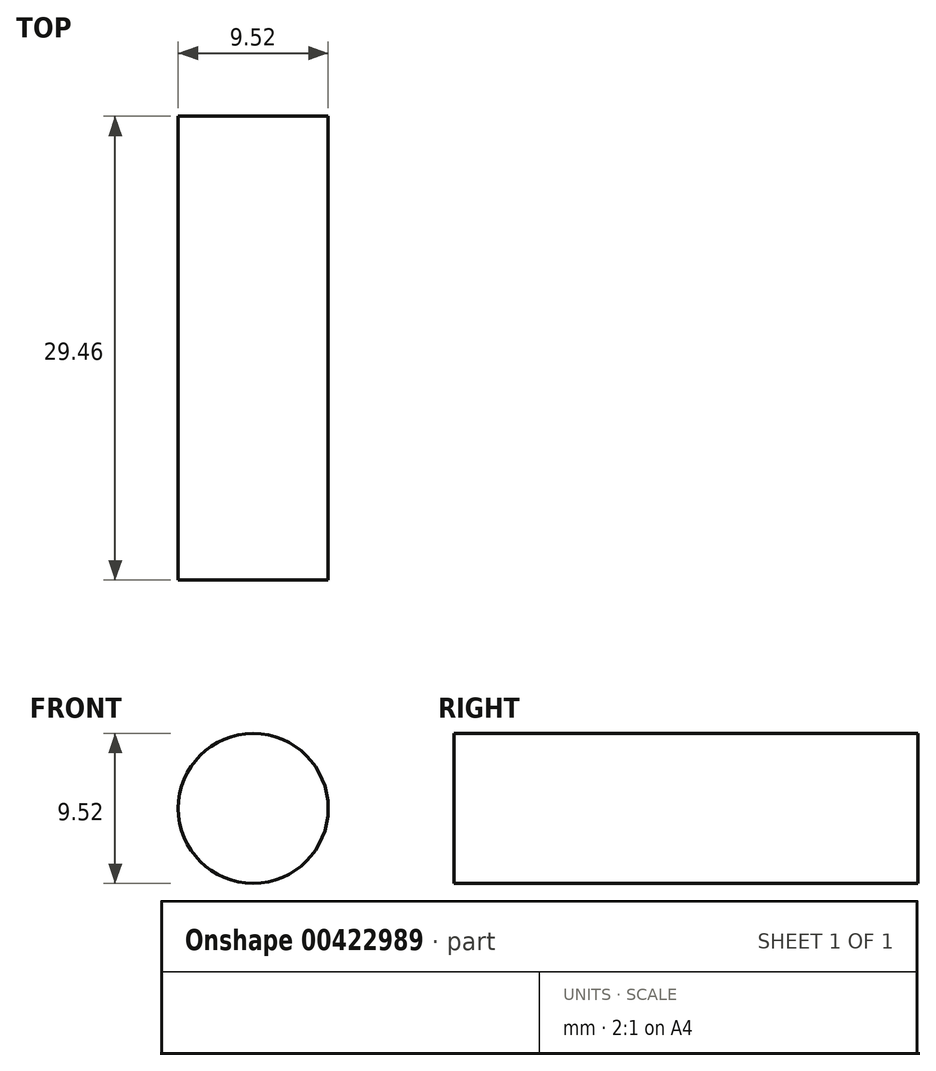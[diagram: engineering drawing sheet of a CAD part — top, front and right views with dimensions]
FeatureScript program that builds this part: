
annotation { "Feature Type Name" : "Feature", "Feature Type Description" : "" }
export const myFeature = defineFeature(function(context is Context, id is Id, definition is map)
    precondition{}
    {
        {
            var Q0;
            Q0=qCreatedBy(makeId("Front.planeOp"),FACE);
            var sketch = newSketch(context, id + "F0", { "sketchPlane" : qUnion([Q0])});
            skCircle(sketch, "E0", {"center": v(0, 0) * mm, "radius": 4.76 * mm});
            skSolve(sketch);
        }
        {
            var Q0;
            Q0 = qSketchRegion(id + "F0", true);
            extrude(context, id + "F1", {"entities" : qUnion([Q0]), "endBound" : BoundingType.SYMMETRIC, "depth" : 29.46 * mm});
        }
    });
